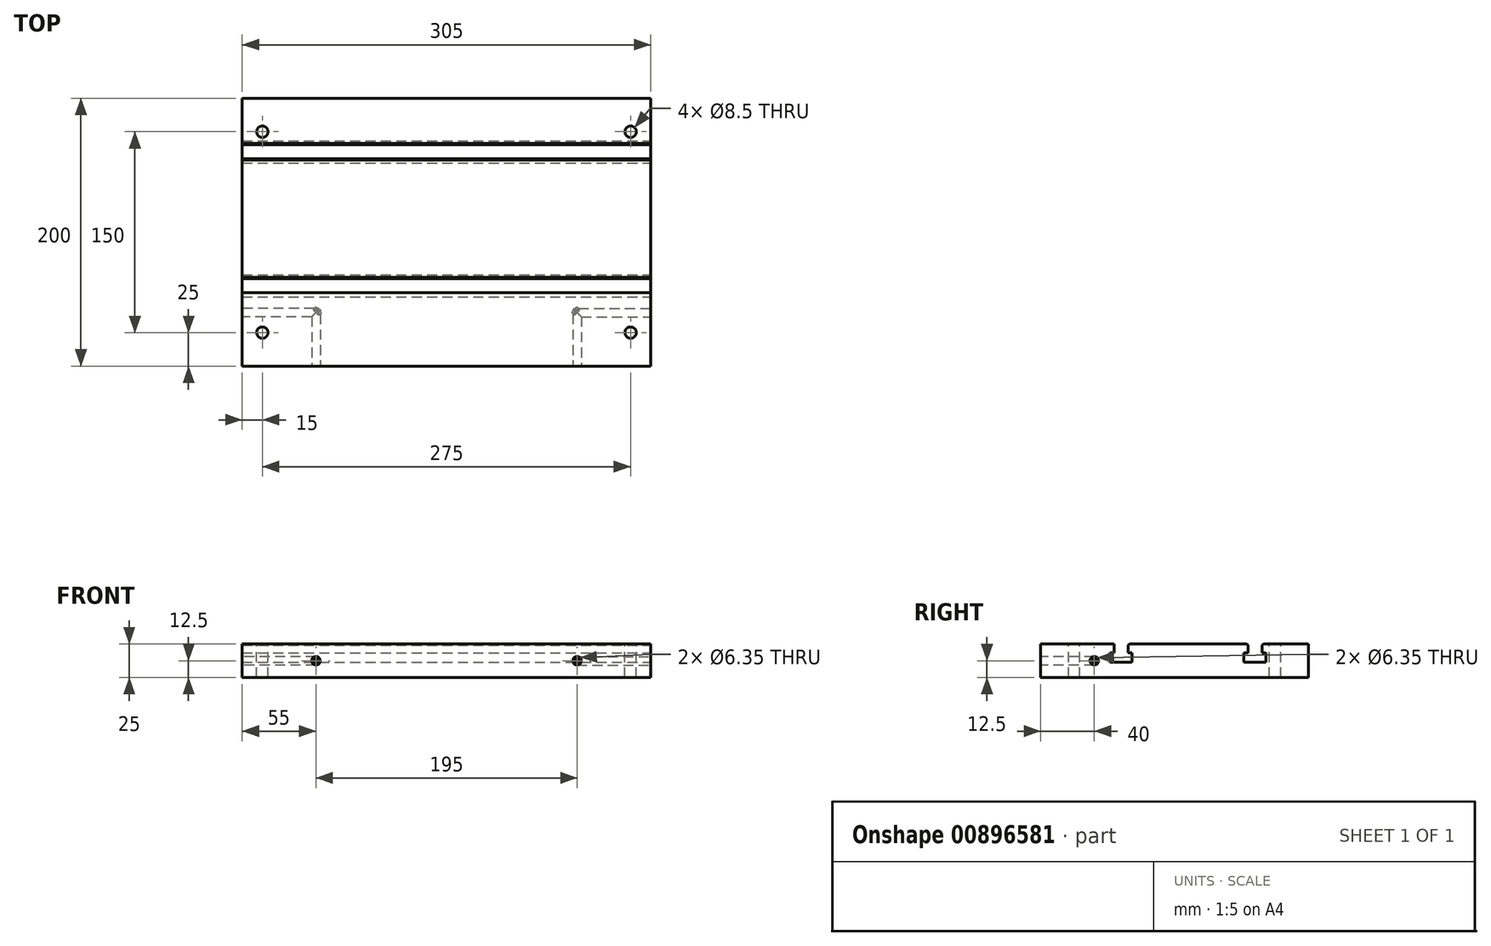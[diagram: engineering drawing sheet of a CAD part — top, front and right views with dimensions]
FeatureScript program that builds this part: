
annotation { "Feature Type Name" : "Feature", "Feature Type Description" : "" }
export const myFeature = defineFeature(function(context is Context, id is Id, definition is map)
    precondition{}
    {
        {
            var Q0;
            Q0=qCreatedBy(makeId("Top.planeOp"),FACE);
            var sketch = newSketch(context, id + "F0", { "sketchPlane" : qUnion([Q0])});
            skLineSegment(sketch, "E0.bottom", {"start": v(-152.5, 100) * mm, "end": v(152.5, 100) * mm});
            skLineSegment(sketch, "E0.top", {"start": v(-152.5, -100) * mm, "end": v(152.5, -100) * mm});
            skLineSegment(sketch, "E0.left", {"start": v(-152.5, 100) * mm, "end": v(-152.5, -100) * mm});
            skLineSegment(sketch, "E0.right", {"start": v(152.5, 100) * mm, "end": v(152.5, -100) * mm});
            skPoint(sketch, "E0.middle", {"position": v(0, 0) * mm});
            skSolve(sketch);
        }
        {
            var Q0;
            Q0=makeQuery(id+"F0.imprint","IMPRINT",FACE,{"disambiguationData":[TD([[makeQuery(id+"F0.imprint","IMPRINT",EDGE,{"derivedFrom":sQuery(id+"F0.wireOp",EDGE,"E0.bottom")}),-1.0]])]});
            extrude(context, id + "F1", {"entities" : qUnion([Q0]), "oppositeDirection" : true, "depth" : 25 * mm, "offsetDistance" : 25 * mm});
        }
        {
            var Q0;
            Q0=makeQuery(id+"F1.opExtrude","CAP_FACE",FACE,{"disambiguationData":[OSD([sQuery(id+"F0.wireOp",EDGE,"E0.bottom"),sQuery(id+"F0.wireOp",EDGE,"E0.top"),sQuery(id+"F0.wireOp",EDGE,"E0.left"),sQuery(id+"F0.wireOp",EDGE,"E0.right")])],"isStart":true});
            var sketch = newSketch(context, id + "F2", { "sketchPlane" : qUnion([Q0])});
            skLineSegment(sketch, "E1.bottom", {"start": v(-137.5, 75) * mm, "end": v(137.5, 75) * mm, "construction": true});
            skLineSegment(sketch, "E1.top", {"start": v(-137.5, -75) * mm, "end": v(137.5, -75) * mm, "construction": true});
            skLineSegment(sketch, "E1.left", {"start": v(-137.5, 75) * mm, "end": v(-137.5, -75) * mm, "construction": true});
            skLineSegment(sketch, "E1.right", {"start": v(137.5, 75) * mm, "end": v(137.5, -75) * mm, "construction": true});
            skPoint(sketch, "E1.middle", {"position": v(0, 0) * mm});
            skSolve(sketch);
        }
        {
            var Q0;
            Q0=sQuery(id+"F2.wireOp",VERTEX,"E1.bottom.start");
            var Q1;
            Q1=sQuery(id+"F2.wireOp",VERTEX,"E1.bottom.end");
            var Q2;
            Q2=sQuery(id+"F2.wireOp",VERTEX,"E1.top.end");
            var Q3;
            Q3=sQuery(id+"F2.wireOp",VERTEX,"E1.top.start");
            var Q4;
            Q4=makeQuery(id+"F1.opExtrude","SWEPT_BODY",BODY,{"disambiguationData":[OSD([sQuery(id+"F0.wireOp",EDGE,"E0.bottom"),sQuery(id+"F0.wireOp",EDGE,"E0.top"),sQuery(id+"F0.wireOp",EDGE,"E0.left"),sQuery(id+"F0.wireOp",EDGE,"E0.right")])]});
            hole(context, id + "F3", {"style" : HoleStyle.SIMPLE, "endStyle" : HoleEndStyle.THROUGH, "standardTappedOrClearance" : lookupTablePath({ "standard" : "ISO", "engagement" : "75%", "pitch" : "1.5 mm", "size" : "M10", "type" : "Tapped" }), "standardBlindInLast" : lookupTablePath({ "standard" : "ISO", "engagement" : "75%", "pitch" : "1.5 mm", "size" : "M10", "type" : "Tapped" }), "holeDiameter" : 8.5 * mm, "majorDiameter" : 10 * mm, "showTappedDepth" : true, "isTappedThrough" : true, "tappedDepth" : 12 * mm, "tapClearance" : 3, "locations" : qUnion([Q0, Q1, Q2, Q3]), "scope" : qUnion([Q4])});
        }
        {
            var Q0;
            Q0=qCreatedBy(makeId("Right.planeOp"),FACE);
            var sketch = newSketch(context, id + "F4", { "sketchPlane" : qUnion([Q0])});
            skLineSegment(sketch, "E2", {"start": v(-40, 0) * mm, "end": v(-40, -25) * mm, "construction": true});
            skLineSegment(sketch, "E3", {"start": v(-40, 0) * mm, "end": v(-34.75, 0) * mm});
            skLineSegment(sketch, "E4", {"start": v(-34.75, 0) * mm, "end": v(-34.75, -6.5) * mm});
            skLineSegment(sketch, "E5", {"start": v(-34.75, -6.5) * mm, "end": v(-31.75, -6.5) * mm});
            skLineSegment(sketch, "E6", {"start": v(-31.75, -6.5) * mm, "end": v(-31.75, -13.5) * mm});
            skLineSegment(sketch, "E7", {"start": v(-31.75, -13.5) * mm, "end": v(-40, -13.5) * mm});
            skLineSegment(sketch, "E8.MirrorCS", {"start": v(-40, 0) * mm, "end": v(-45.25, 0) * mm});
            skLineSegment(sketch, "E9.MirrorCS", {"start": v(-45.25, 0) * mm, "end": v(-45.25, -6.5) * mm});
            skLineSegment(sketch, "E10.MirrorCS", {"start": v(-45.25, -6.5) * mm, "end": v(-48.25, -6.5) * mm});
            skLineSegment(sketch, "E11.MirrorCS", {"start": v(-48.25, -6.5) * mm, "end": v(-48.25, -13.5) * mm});
            skLineSegment(sketch, "E12.MirrorCS", {"start": v(-48.25, -13.5) * mm, "end": v(-40, -13.5) * mm});
            skLineSegment(sketch, "E13", {"start": v(60, 0) * mm, "end": v(60, -25) * mm, "construction": true});
            skLineSegment(sketch, "E14", {"start": v(60, 0) * mm, "end": v(65.25, 0) * mm});
            skLineSegment(sketch, "E15", {"start": v(65.25, 0) * mm, "end": v(65.25, -6.5) * mm});
            skLineSegment(sketch, "E16", {"start": v(65.25, -6.5) * mm, "end": v(68.25, -6.5) * mm});
            skLineSegment(sketch, "E17", {"start": v(68.25, -6.5) * mm, "end": v(68.25, -13.5) * mm});
            skLineSegment(sketch, "E18", {"start": v(68.25, -13.5) * mm, "end": v(60, -13.5) * mm});
            skLineSegment(sketch, "E19.MirrorCS", {"start": v(60, 0) * mm, "end": v(54.75, 0) * mm});
            skLineSegment(sketch, "E20.MirrorCS", {"start": v(54.75, 0) * mm, "end": v(54.75, -6.5) * mm});
            skLineSegment(sketch, "E21.MirrorCS", {"start": v(54.75, -6.5) * mm, "end": v(51.75, -6.5) * mm});
            skLineSegment(sketch, "E22.MirrorCS", {"start": v(51.75, -6.5) * mm, "end": v(51.75, -13.5) * mm});
            skLineSegment(sketch, "E23.MirrorCS", {"start": v(51.75, -13.5) * mm, "end": v(60, -13.5) * mm});
            skSolve(sketch);
        }
        {
            var Q0;
            Q0 = qSketchRegion(id + "F4", true);
            extrude(context, id + "F5", {"entities" : qUnion([Q0]), "operationType" : NewBodyOperationType.REMOVE, "endBound" : BoundingType.THROUGH_ALL, "oppositeDirection" : true, "depth" : 25 * mm, "offsetDistance" : 25 * mm, "hasSecondDirection" : true, "secondDirectionBound" : SecondDirectionBoundingType.THROUGH_ALL, "secondDirectionOppositeDirection" : false, "secondDirectionDepth" : 25 * mm});
        }
        {
            var Q0;
            Q0=makeQuery(id+"F5.boolean.opBoolean","COPY",EDGE,{"derivedFrom":makeQuery(id+"F5.opExtrude","SWEPT_EDGE",EDGE,{"disambiguationData":[OSD([sQuery(id+"F4.wireOp",EDGE,"E3"),sQuery(id+"F4.wireOp",EDGE,"E4")])]})});
            var Q1;
            Q1=makeQuery(id+"F5.boolean.opBoolean","COPY",EDGE,{"derivedFrom":makeQuery(id+"F5.opExtrude","SWEPT_EDGE",EDGE,{"disambiguationData":[OSD([sQuery(id+"F4.wireOp",EDGE,"E8.MirrorCS"),sQuery(id+"F4.wireOp",EDGE,"E9.MirrorCS")])]})});
            var Q2;
            Q2=makeQuery(id+"F5.boolean.opBoolean","COPY",EDGE,{"derivedFrom":makeQuery(id+"F5.opExtrude","SWEPT_EDGE",EDGE,{"disambiguationData":[OSD([sQuery(id+"F4.wireOp",EDGE,"E14"),sQuery(id+"F4.wireOp",EDGE,"E15")])]})});
            var Q3;
            Q3=makeQuery(id+"F5.boolean.opBoolean","COPY",EDGE,{"derivedFrom":makeQuery(id+"F5.opExtrude","SWEPT_EDGE",EDGE,{"disambiguationData":[OSD([sQuery(id+"F4.wireOp",EDGE,"E19.MirrorCS"),sQuery(id+"F4.wireOp",EDGE,"E20.MirrorCS")])]})});
            chamfer(context, id + "F6", {"entities" : qUnion([Q0, Q1, Q2, Q3]), "width" : 1 * mm, "tangentPropagation" : true});
        }
        {
            var Q0;
            Q0=makeQuery(id+"F1.opExtrude","SWEPT_FACE",FACE,{"disambiguationData":[OSD([sQuery(id+"F0.wireOp",EDGE,"E0.left")])]});
            var sketch = newSketch(context, id + "F7", { "sketchPlane" : qUnion([Q0])});
            skPoint(sketch, "E24", {"position": v(60, -12.5) * mm});
            skSolve(sketch);
        }
        {
            var Q0;
            Q0=makeQuery(id+"F1.opExtrude","SWEPT_FACE",FACE,{"disambiguationData":[OSD([sQuery(id+"F0.wireOp",EDGE,"E0.right")])]});
            var sketch = newSketch(context, id + "F8", { "sketchPlane" : qUnion([Q0])});
            skPoint(sketch, "E25.0", {"position": v(-60, -12.5) * mm});
            skSolve(sketch);
        }
        {
            var Q0;
            Q0=makeQuery(id+"F1.opExtrude","SWEPT_FACE",FACE,{"disambiguationData":[OSD([sQuery(id+"F0.wireOp",EDGE,"E0.top")])]});
            var sketch = newSketch(context, id + "F9", { "sketchPlane" : qUnion([Q0])});
            skPoint(sketch, "E26", {"position": v(-97.5, -12.5) * mm});
            skPoint(sketch, "E27.MirrorP", {"position": v(97.5, -12.5) * mm});
            skSolve(sketch);
        }
        {
            var Q0;
            Q0=sQuery(id+"F9.wireOp",VERTEX,"E27.MirrorP");
            var Q1;
            Q1=sQuery(id+"F9.wireOp",VERTEX,"E26");
            var Q2;
            Q2=makeQuery(id+"F1.opExtrude","SWEPT_BODY",BODY,{"disambiguationData":[OSD([sQuery(id+"F0.wireOp",EDGE,"E0.bottom"),sQuery(id+"F0.wireOp",EDGE,"E0.top"),sQuery(id+"F0.wireOp",EDGE,"E0.left"),sQuery(id+"F0.wireOp",EDGE,"E0.right")])]});
            hole(context, id + "F10", {"style" : HoleStyle.SIMPLE, "endStyle" : HoleEndStyle.BLIND, "holeDiameter" : 6.35 * mm, "majorDiameter" : 10 * mm, "holeDepth" : 42 * mm, "isTappedThrough" : true, "tappedDepth" : 12 * mm, "tapClearance" : 3, "locations" : qUnion([Q0, Q1]), "scope" : qUnion([Q2])});
        }
        {
            var Q0;
            Q0=sQuery(id+"F7.wireOp",VERTEX,"E24");
            var Q1;
            Q1=sQuery(id+"F8.wireOp",VERTEX,"E25.0");
            var Q2;
            Q2=makeQuery(id+"F1.opExtrude","SWEPT_BODY",BODY,{"disambiguationData":[OSD([sQuery(id+"F0.wireOp",EDGE,"E0.bottom"),sQuery(id+"F0.wireOp",EDGE,"E0.top"),sQuery(id+"F0.wireOp",EDGE,"E0.left"),sQuery(id+"F0.wireOp",EDGE,"E0.right")])]});
            hole(context, id + "F11", {"style" : HoleStyle.SIMPLE, "endStyle" : HoleEndStyle.BLIND, "holeDiameter" : 6.35 * mm, "majorDiameter" : 5 * mm, "holeDepth" : 57 * mm, "isTappedThrough" : true, "tappedDepth" : 12 * mm, "tapClearance" : 3, "locations" : qUnion([Q0, Q1]), "scope" : qUnion([Q2])});
        }
    });
